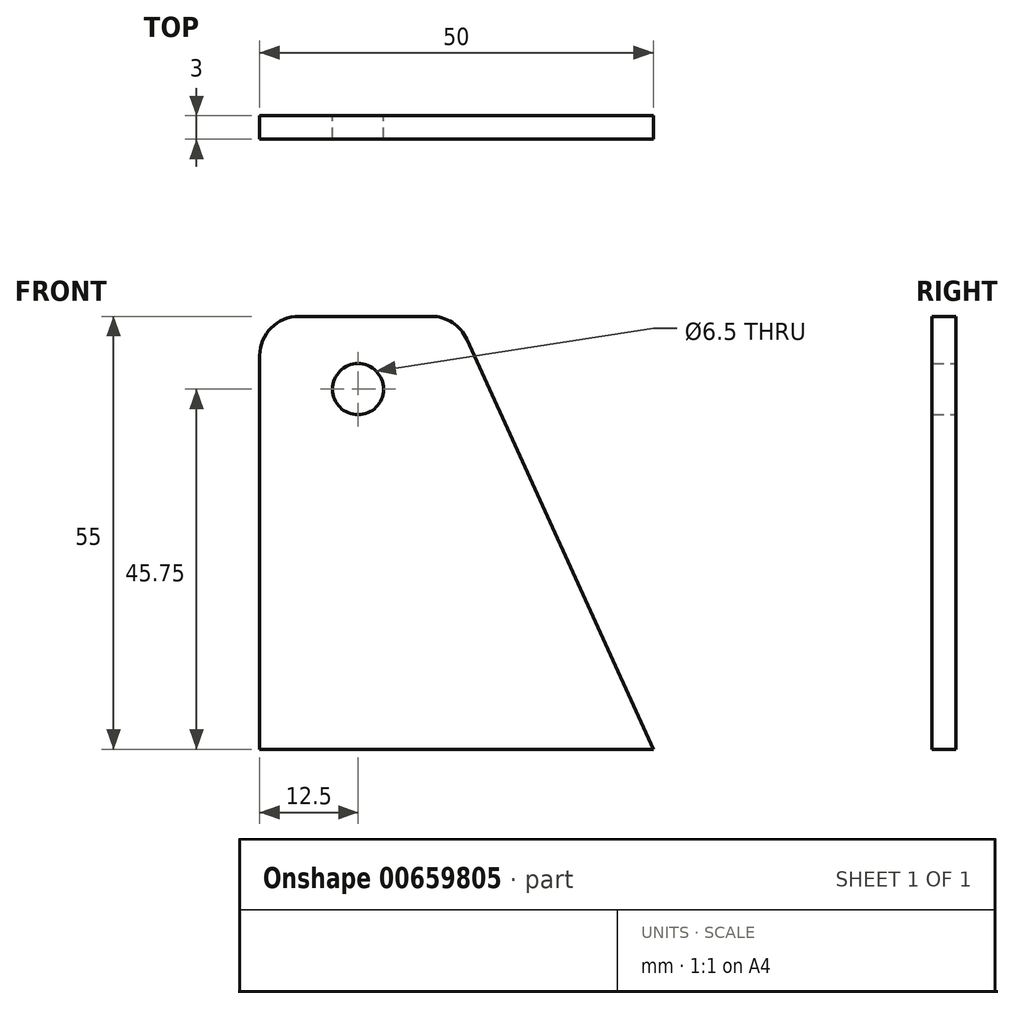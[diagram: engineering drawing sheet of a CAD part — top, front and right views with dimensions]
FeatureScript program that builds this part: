
annotation { "Feature Type Name" : "Feature", "Feature Type Description" : "" }
export const myFeature = defineFeature(function(context is Context, id is Id, definition is map)
    precondition{}
    {
        {
            var Q0;
            Q0=qCreatedBy(makeId("Front.planeOp"),FACE);
            var sketch = newSketch(context, id + "F0", { "sketchPlane" : qUnion([Q0])});
            skLineSegment(sketch, "E0.bottom", {"start": v(7.5, 27.5) * mm, "end": v(-7.5, 27.5) * mm});
            skLineSegment(sketch, "E0.top", {"start": v(12.5, -27.5) * mm, "end": v(-12.5, -27.5) * mm});
            skLineSegment(sketch, "E0.right", {"start": v(-12.5, 22.5) * mm, "end": v(-12.5, -27.5) * mm});
            skCircle(sketch, "E1", {"center": v(0, 18.25) * mm, "radius": 3.25 * mm});
            skPoint(sketch, "E2.visualSharp", {"position": v(-12.5, 27.5) * mm});
            skArc(sketch, "E2.filletArc", {"start": v(-7.5, 27.5) * mm, "mid": v(-11.04, 26.04) * mm, "end": v(-12.5, 22.5) * mm});
            skPoint(sketch, "E3.visualSharp", {"position": v(12.5, 27.5) * mm});
            skLineSegment(sketch, "E4", {"start": v(12.5, -27.5) * mm, "end": v(37.5, -27.5) * mm});
            skLineSegment(sketch, "E5", {"start": v(7.5, 27.5) * mm, "end": v(9.28, 27.5) * mm});
            skLineSegment(sketch, "E6", {"start": v(37.5, -27.5) * mm, "end": v(13.83, 24.57) * mm});
            skArc(sketch, "E7.filletArc", {"start": v(13.83, 24.57) * mm, "mid": v(11.99, 26.7) * mm, "end": v(9.28, 27.5) * mm});
            skSolve(sketch);
        }
        {
            var Q0;
            Q0=makeQuery(id+"F0.imprint","IMPRINT",FACE,{"disambiguationData":[TD([[makeQuery(id+"F0.imprint","IMPRINT",EDGE,{"derivedFrom":sQuery(id+"F0.wireOp",EDGE,"E0.bottom")}),1.0]])]});
            extrude(context, id + "F1", {"entities" : qUnion([Q0]), "depth" : 3 * mm, "offsetDistance" : 25 * mm});
        }
    });
